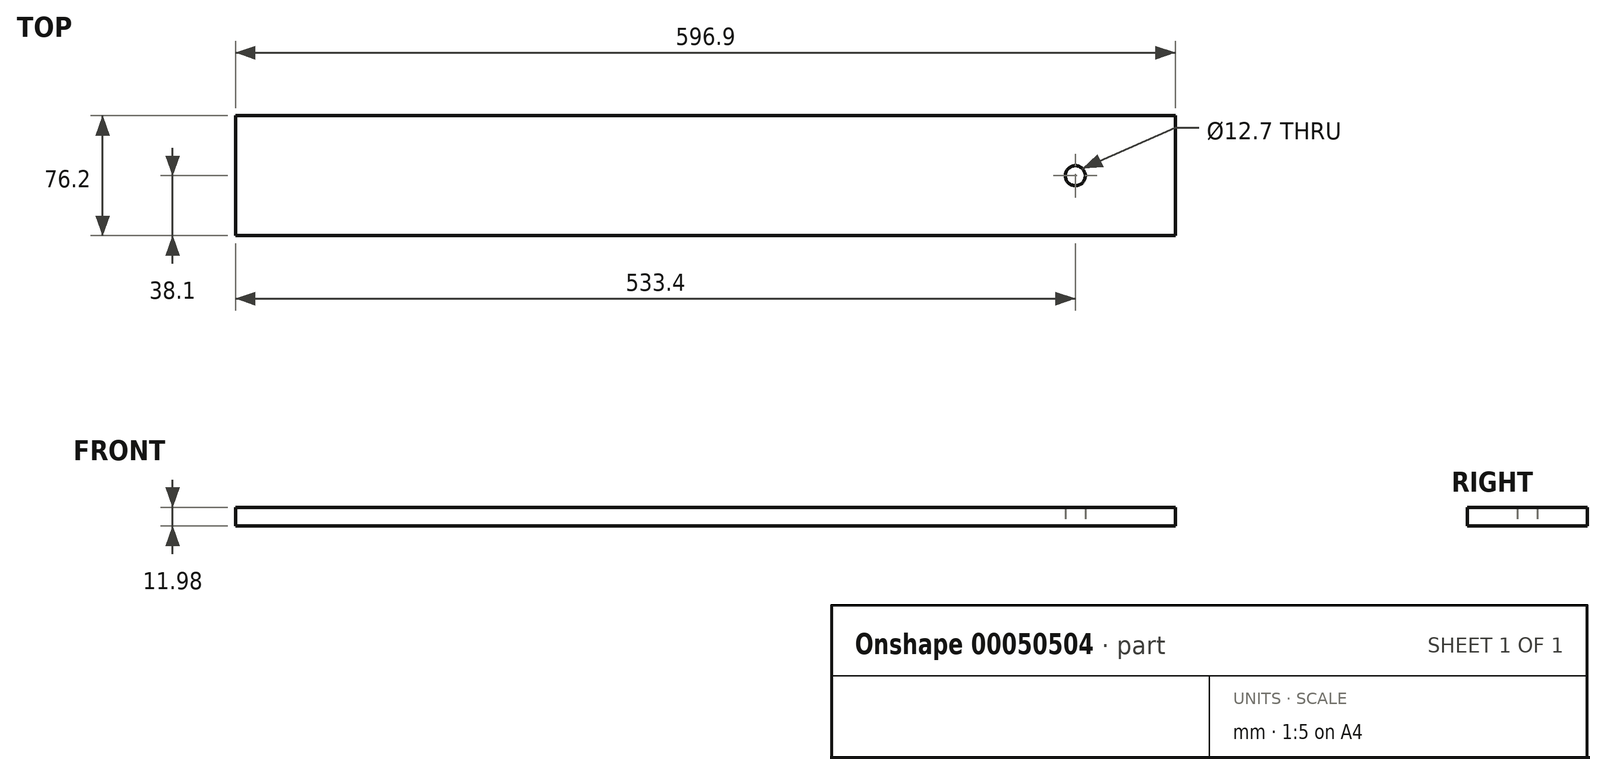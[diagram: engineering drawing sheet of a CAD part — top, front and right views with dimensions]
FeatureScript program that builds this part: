
annotation { "Feature Type Name" : "Feature", "Feature Type Description" : "" }
export const myFeature = defineFeature(function(context is Context, id is Id, definition is map)
    precondition{}
    {
        {
            var Q0;
            Q0=qCreatedBy(makeId("Top.planeOp"),FACE);
            var sketch = newSketch(context, id + "F0", { "sketchPlane" : qUnion([Q0])});
            skLineSegment(sketch, "E0.rect.bottom", {"start": v(387.35, 38.1) * mm, "end": v(-387.35, 38.1) * mm});
            skLineSegment(sketch, "E0.rect.top", {"start": v(387.35, -38.1) * mm, "end": v(-387.35, -38.1) * mm});
            skLineSegment(sketch, "E0.rect.left", {"start": v(387.35, 38.1) * mm, "end": v(387.35, -38.1) * mm});
            skLineSegment(sketch, "E0.rect.right", {"start": v(-387.35, 38.1) * mm, "end": v(-387.35, -38.1) * mm});
            skPoint(sketch, "E0.rect.middle", {"position": v(0, 0) * mm});
            skSolve(sketch);
        }
        {
            var Q0;
            Q0=qSketchRegion(id+"F0",true);
            extrude(context, id + "F1", {"entities" : qUnion([Q0]), "endBound" : BoundingType.SYMMETRIC, "depth" : 12 * mm});
        }
        {
            var Q0;
            Q0=makeQuery(id+"F1.opExtrude","CAP_FACE",FACE,{"disambiguationData":[OSD([sQuery(id+"F0.wireOp",EDGE,"E0.rect.bottom"),sQuery(id+"F0.wireOp",EDGE,"E0.rect.top"),sQuery(id+"F0.wireOp",EDGE,"E0.rect.left"),sQuery(id+"F0.wireOp",EDGE,"E0.rect.right")])],"isStart":true});
            var sketch = newSketch(context, id + "F2", { "sketchPlane" : qUnion([Q0])});
            skCircle(sketch, "E1", {"center": v(-316.7, 0) * mm, "radius": 6.35 * mm});
            skCircle(sketch, "E2", {"center": v(323.85, 0) * mm, "radius": 6.35 * mm});
            skSolve(sketch);
        }
        {
            var Q0;
            Q0=qSketchRegion(id+"F2",true);
            extrude(context, id + "F3", {"entities" : qUnion([Q0]), "operationType" : NewBodyOperationType.REMOVE, "endBound" : BoundingType.UP_TO_NEXT, "oppositeDirection" : true, "depth" : 25.4 * mm});
        }
        {
            var Q0;
            Q0=makeQuery(id+"F1.opExtrude","CAP_FACE",FACE,{"disambiguationData":[OSD([sQuery(id+"F0.wireOp",EDGE,"E0.rect.bottom"),sQuery(id+"F0.wireOp",EDGE,"E0.rect.top"),sQuery(id+"F0.wireOp",EDGE,"E0.rect.left"),sQuery(id+"F0.wireOp",EDGE,"E0.rect.right")])],"isStart":false});
            var sketch = newSketch(context, id + "F4", { "sketchPlane" : qUnion([Q0])});
            skLineSegment(sketch, "E3.bottom", {"start": v(-349.25, 0) * mm, "end": v(-234.95, 0) * mm, "construction": true});
            skCircle(sketch, "E4", {"center": v(-349.25, 0) * mm, "radius": 6.35 * mm});
            skCircle(sketch, "E5", {"center": v(-234.95, 0) * mm, "radius": 6.35 * mm});
            skLineSegment(sketch, "E6", {"start": v(-316.7, 0) * mm, "end": v(-292.1, 0) * mm, "construction": true});
            skSolve(sketch);
        }
        {
            var Q0;
            Q0=qSketchRegion(id+"F4",true);
            extrude(context, id + "F5", {"entities" : qUnion([Q0]), "operationType" : NewBodyOperationType.REMOVE, "endBound" : BoundingType.UP_TO_NEXT, "oppositeDirection" : true, "depth" : 25.4 * mm});
        }
        {
            var Q0;
            Q0=makeQuery(id+"F1.opExtrude","CAP_FACE",FACE,{"disambiguationData":[OSD([sQuery(id+"F0.wireOp",EDGE,"E0.rect.bottom"),sQuery(id+"F0.wireOp",EDGE,"E0.rect.top"),sQuery(id+"F0.wireOp",EDGE,"E0.rect.left"),sQuery(id+"F0.wireOp",EDGE,"E0.rect.right")])],"isStart":false});
            var sketch = newSketch(context, id + "F6", { "sketchPlane" : qUnion([Q0])});
            skLineSegment(sketch, "E7.bottom", {"start": v(-387.35, 38.1) * mm, "end": v(-209.55, 38.1) * mm});
            skLineSegment(sketch, "E7.top", {"start": v(-387.35, -38.1) * mm, "end": v(-209.55, -38.1) * mm});
            skLineSegment(sketch, "E7.left", {"start": v(-209.55, 38.1) * mm, "end": v(-209.55, -38.1) * mm});
            skLineSegment(sketch, "E7.right", {"start": v(-387.35, 38.1) * mm, "end": v(-387.35, -38.1) * mm});
            skSolve(sketch);
        }
        {
            var Q0;
            Q0 = qSketchRegion(id + "F6", true);
            extrude(context, id + "F7", {"entities" : qUnion([Q0]), "operationType" : NewBodyOperationType.REMOVE, "endBound" : BoundingType.UP_TO_NEXT, "oppositeDirection" : true, "depth" : 25.4 * mm});
        }
    });
